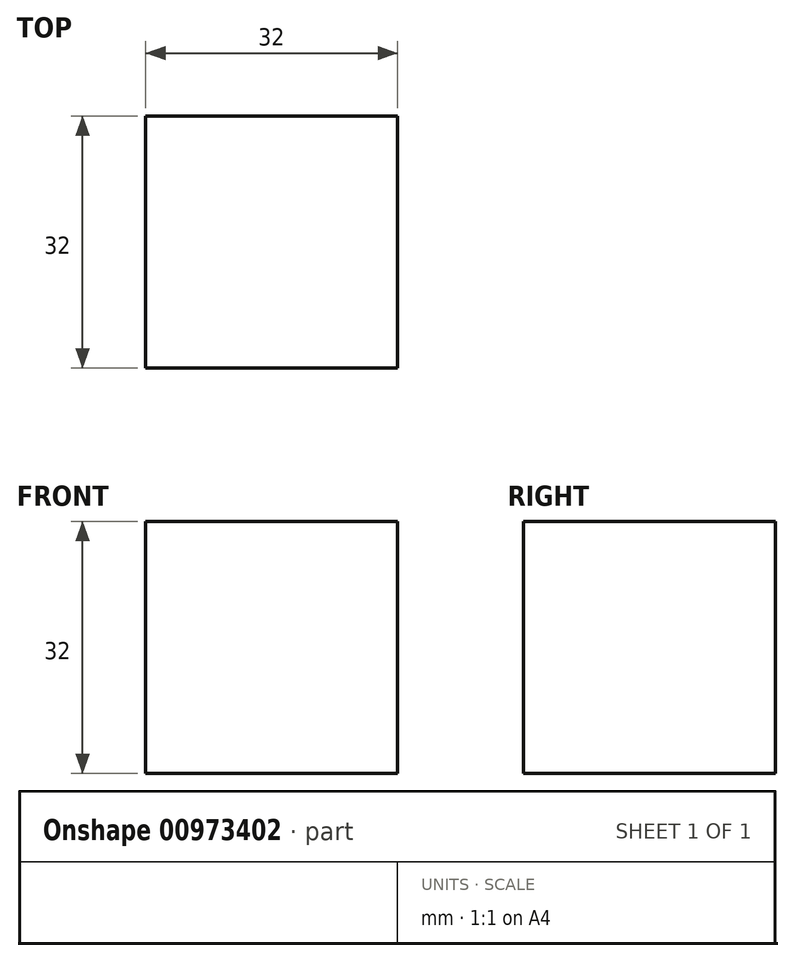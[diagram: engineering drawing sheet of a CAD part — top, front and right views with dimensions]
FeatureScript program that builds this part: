
annotation { "Feature Type Name" : "Feature", "Feature Type Description" : "" }
export const myFeature = defineFeature(function(context is Context, id is Id, definition is map)
    precondition{}
    {
        {
            var Q0;
            Q0=qCreatedBy(makeId("Top.planeOp"),FACE);
            var sketch = newSketch(context, id + "F0", { "sketchPlane" : qUnion([Q0])});
            skLineSegment(sketch, "E0.bottom", {"start": v(0, 0) * mm, "end": v(-32, 0) * mm});
            skLineSegment(sketch, "E0.top", {"start": v(0, -32) * mm, "end": v(-32, -32) * mm});
            skLineSegment(sketch, "E0.left", {"start": v(0, 0) * mm, "end": v(0, -32) * mm});
            skLineSegment(sketch, "E0.right", {"start": v(-32, 0) * mm, "end": v(-32, -32) * mm});
            skSolve(sketch);
        }
        {
            var Q0;
            Q0 = qSketchRegion(id + "F0", true);
            extrude(context, id + "F1", {"entities" : qUnion([Q0]), "depth" : 32 * mm, "offsetDistance" : 25 * mm});
        }
    });
